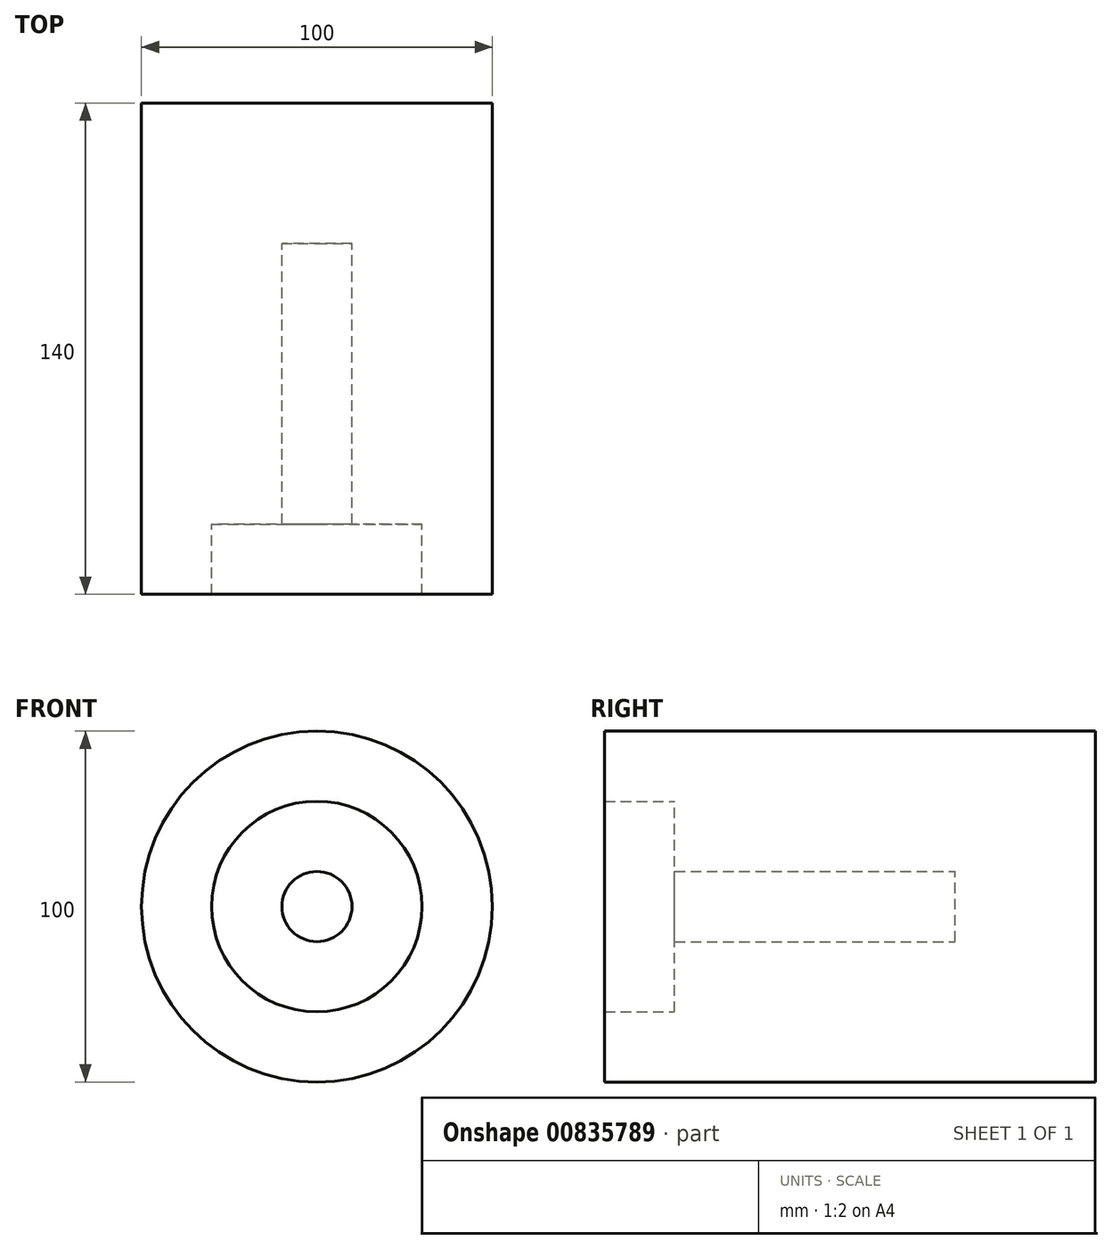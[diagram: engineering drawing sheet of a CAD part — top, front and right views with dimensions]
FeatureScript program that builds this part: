
annotation { "Feature Type Name" : "Feature", "Feature Type Description" : "" }
export const myFeature = defineFeature(function(context is Context, id is Id, definition is map)
    precondition{}
    {
        {
            var Q0;
            Q0=qCreatedBy(makeId("Front.planeOp"),FACE);
            var sketch = newSketch(context, id + "F0", { "sketchPlane" : qUnion([Q0])});
            skCircle(sketch, "E0", {"center": v(0.03, 0) * mm, "radius": 10 * mm});
            skCircle(sketch, "E1", {"center": v(0, 0) * mm, "radius": 30 * mm});
            skCircle(sketch, "E2", {"center": v(0.03, 0) * mm, "radius": 50 * mm});
            skSolve(sketch);
        }
        {
            var Q0;
            Q0=makeQuery(id+"F0.imprint","IMPRINT",FACE,{"disambiguationData":[TD([[makeQuery(id+"F0.imprint","IMPRINT",EDGE,{"derivedFrom":sQuery(id+"F0.wireOp",EDGE,"E0")}),1.0]])]});
            var Q1;
            Q1=sQuery(id+"F0.wireOp",EDGE,"E0");
            extrude(context, id + "F1", {"entities" : qUnion([Q0]), "surfaceEntities" : qUnion([Q1]), "depth" : 40 * mm, "offsetDistance" : 25 * mm});
        }
        {
            var Q0;
            Q0=makeQuery(id+"F0.imprint","IMPRINT",FACE,{"disambiguationData":[TD([[makeQuery(id+"F0.imprint","IMPRINT",EDGE,{"derivedFrom":sQuery(id+"F0.wireOp",EDGE,"E0")}),-1.0]])]});
            extrude(context, id + "F2", {"entities" : qUnion([Q0]), "operationType" : NewBodyOperationType.ADD, "depth" : 120 * mm, "offsetDistance" : 25 * mm});
        }
        {
            var Q0;
            Q0=makeQuery(id+"F0.imprint","IMPRINT",FACE,{"disambiguationData":[TD([[makeQuery(id+"F0.imprint","IMPRINT",EDGE,{"derivedFrom":sQuery(id+"F0.wireOp",EDGE,"E1")}),-1.0]])]});
            extrude(context, id + "F3", {"entities" : qUnion([Q0]), "operationType" : NewBodyOperationType.ADD, "depth" : 140 * mm, "offsetDistance" : 25 * mm});
        }
    });
